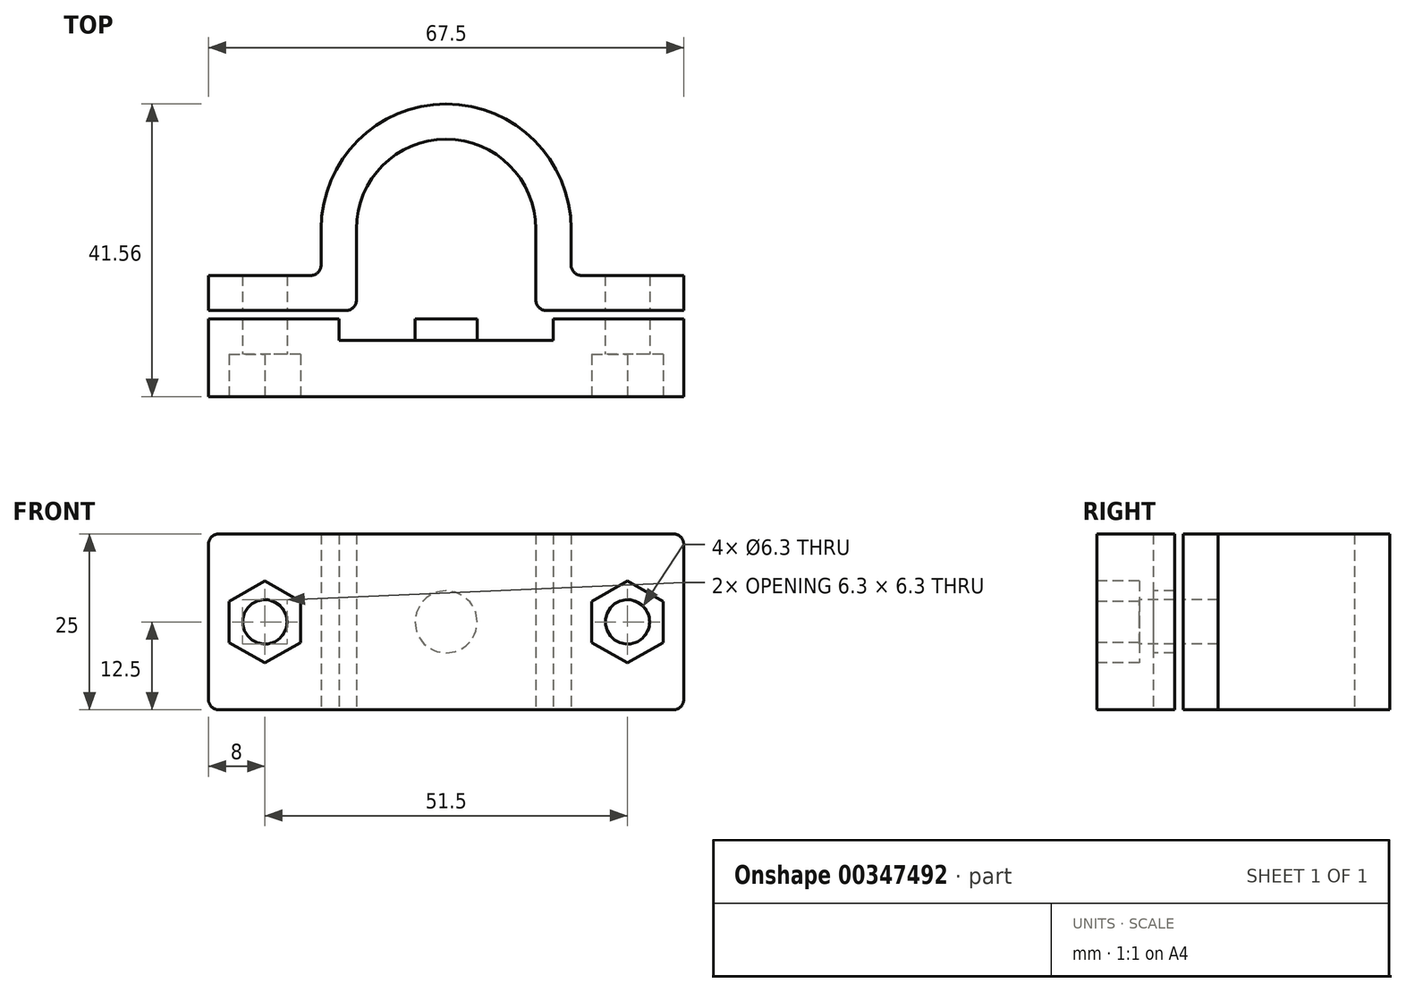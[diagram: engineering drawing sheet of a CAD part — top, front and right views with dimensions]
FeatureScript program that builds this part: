
annotation { "Feature Type Name" : "Feature", "Feature Type Description" : "" }
export const myFeature = defineFeature(function(context is Context, id is Id, definition is map)
    precondition{}
    {
        {
            var Q0;
            Q0=qCreatedBy(makeId("Top.planeOp"),FACE);
            var sketch = newSketch(context, id + "F0", { "sketchPlane" : qUnion([Q0])});
            skArc(sketch, "E0", {"start": v(12.75, 3.02) * mm, "mid": v(0, 15.77) * mm, "end": v(-12.75, 3.03) * mm});
            skLineSegment(sketch, "E1", {"start": v(-12.75, 3.02) * mm, "end": v(-12.75, -8.58) * mm});
            skLineSegment(sketch, "E2", {"start": v(-12.75, -8.58) * mm, "end": v(-33.75, -8.57) * mm});
            skLineSegment(sketch, "E3", {"start": v(-33.75, -8.57) * mm, "end": v(-33.75, -3.58) * mm});
            skLineSegment(sketch, "E4", {"start": v(-33.75, -3.58) * mm, "end": v(-17.75, -3.58) * mm});
            skLineSegment(sketch, "E5", {"start": v(-17.75, -3.58) * mm, "end": v(-17.75, 3.02) * mm});
            skArc(sketch, "E6", {"start": v(17.75, 3.03) * mm, "mid": v(0, 20.78) * mm, "end": v(-17.75, 3.03) * mm});
            skLineSegment(sketch, "E7", {"start": v(17.75, 3.03) * mm, "end": v(17.75, -3.58) * mm});
            skLineSegment(sketch, "E8", {"start": v(17.75, -3.58) * mm, "end": v(33.75, -3.58) * mm});
            skLineSegment(sketch, "E9", {"start": v(33.75, -3.58) * mm, "end": v(33.75, -8.57) * mm});
            skLineSegment(sketch, "E10", {"start": v(33.75, -8.57) * mm, "end": v(12.75, -8.58) * mm});
            skLineSegment(sketch, "E11", {"start": v(12.75, -8.58) * mm, "end": v(12.75, 3.02) * mm});
            skLineSegment(sketch, "E12", {"start": v(-33.75, -9.78) * mm, "end": v(-15.2, -9.78) * mm});
            skLineSegment(sketch, "E13", {"start": v(-15.2, -9.78) * mm, "end": v(-15.2, -12.78) * mm});
            skLineSegment(sketch, "E14", {"start": v(-15.2, -12.78) * mm, "end": v(15.2, -12.78) * mm});
            skLineSegment(sketch, "E15", {"start": v(15.2, -12.78) * mm, "end": v(15.2, -9.78) * mm});
            skLineSegment(sketch, "E16", {"start": v(15.2, -9.78) * mm, "end": v(33.75, -9.77) * mm});
            skLineSegment(sketch, "E17", {"start": v(33.75, -9.77) * mm, "end": v(33.75, -20.77) * mm});
            skLineSegment(sketch, "E18", {"start": v(33.75, -20.77) * mm, "end": v(-33.75, -20.78) * mm});
            skLineSegment(sketch, "E19", {"start": v(-33.75, -20.78) * mm, "end": v(-33.75, -9.78) * mm});
            skSolve(sketch);
        }
        {
            var Q0;
            Q0=makeQuery(id+"F0.imprint","IMPRINT",FACE,{"disambiguationData":[TD([[makeQuery(id+"F0.imprint","IMPRINT",EDGE,{"derivedFrom":sQuery(id+"F0.wireOp",EDGE,"E0")}),-1.0]])]});
            var Q1;
            Q1=makeQuery(id+"F0.imprint","IMPRINT",FACE,{"disambiguationData":[TD([[makeQuery(id+"F0.imprint","IMPRINT",EDGE,{"derivedFrom":sQuery(id+"F0.wireOp",EDGE,"E12")}),-1.0]])]});
            extrude(context, id + "F1", {"entities" : qUnion([Q0, Q1]), "depth" : 25 * mm});
        }
        {
            var Q0;
            Q0=makeQuery(id+"F1.opExtrude","SWEPT_FACE",FACE,{"disambiguationData":[OSD([sQuery(id+"F0.wireOp",EDGE,"E18")])]});
            var sketch = newSketch(context, id + "F2", { "sketchPlane" : qUnion([Q0])});
            skCircle(sketch, "E20", {"center": v(-25.75, 12.5) * mm, "radius": 3.15 * mm});
            skCircle(sketch, "E21", {"center": v(25.75, 12.5) * mm, "radius": 3.15 * mm});
            skSolve(sketch);
        }
        {
            var Q0;
            Q0=makeQuery(id+"F2.imprint","IMPRINT",FACE,{"disambiguationData":[TD([[makeQuery(id+"F2.imprint","IMPRINT",EDGE,{"derivedFrom":sQuery(id+"F2.wireOp",EDGE,"E20")}),1.0]])]});
            var Q1;
            Q1=makeQuery(id+"F2.imprint","IMPRINT",FACE,{"disambiguationData":[TD([[makeQuery(id+"F2.imprint","IMPRINT",EDGE,{"derivedFrom":sQuery(id+"F2.wireOp",EDGE,"E21")}),1.0]])]});
            extrude(context, id + "F3", {"entities" : qUnion([Q0, Q1]), "operationType" : NewBodyOperationType.REMOVE, "oppositeDirection" : true, "depth" : 25 * mm});
        }
        {
            var Q0;
            Q0=makeQuery(id+"F1.opExtrude","SWEPT_FACE",FACE,{"disambiguationData":[OSD([sQuery(id+"F0.wireOp",EDGE,"E14")])]});
            var sketch = newSketch(context, id + "F4", { "sketchPlane" : qUnion([Q0])});
            skCircle(sketch, "E22", {"center": v(0, 12.5) * mm, "radius": 4.4 * mm});
            skSolve(sketch);
        }
        {
            var Q0;
            Q0=makeQuery(id+"F4.imprint","IMPRINT",FACE,{"disambiguationData":[TD([[makeQuery(id+"F4.imprint","IMPRINT",EDGE,{"derivedFrom":sQuery(id+"F4.wireOp",EDGE,"E22")}),1.0]])]});
            extrude(context, id + "F5", {"entities" : qUnion([Q0]), "operationType" : NewBodyOperationType.ADD, "depth" : 3 * mm});
        }
        {
            var Q0;
            Q0=makeQuery(id+"F1.opExtrude","SWEPT_FACE",FACE,{"disambiguationData":[OSD([sQuery(id+"F0.wireOp",EDGE,"E2")])]});
            var sketch = newSketch(context, id + "F6", { "sketchPlane" : qUnion([Q0])});
            skCircle(sketch, "E23", {"center": v(25.75, 12.5) * mm, "radius": 3.1 * mm});
            skCircle(sketch, "E24", {"center": v(-25.75, 12.5) * mm, "radius": 3.1 * mm});
            skSolve(sketch);
        }
        {
            var Q0;
            Q0=makeQuery(id+"F6.imprint","IMPRINT",FACE,{"disambiguationData":[TD([[makeQuery(id+"F6.imprint","IMPRINT",EDGE,{"derivedFrom":sQuery(id+"F6.wireOp",EDGE,"E24")}),1.0]])]});
            var Q1;
            Q1=makeQuery(id+"F6.imprint","IMPRINT",FACE,{"disambiguationData":[TD([[makeQuery(id+"F6.imprint","IMPRINT",EDGE,{"derivedFrom":sQuery(id+"F6.wireOp",EDGE,"E23")}),1.0]])]});
            extrude(context, id + "F7", {"entities" : qUnion([Q0, Q1]), "operationType" : NewBodyOperationType.REMOVE, "oppositeDirection" : true, "depth" : 25 * mm});
        }
        {
            var Q0;
            Q0=makeQuery(id+"F1.opExtrude","SWEPT_EDGE",EDGE,{"disambiguationData":[OSD([sQuery(id+"F0.wireOp",EDGE,"E4"),sQuery(id+"F0.wireOp",EDGE,"E5")])]});
            var Q1;
            Q1=makeQuery(id+"F1.opExtrude","SWEPT_EDGE",EDGE,{"disambiguationData":[OSD([sQuery(id+"F0.wireOp",EDGE,"E7"),sQuery(id+"F0.wireOp",EDGE,"E8")])]});
            var Q2;
            Q2=makeQuery(id+"F1.opExtrude","CAP_EDGE",EDGE,{"disambiguationData":[OSD([sQuery(id+"F0.wireOp",EDGE,"E9")])],"isStart":false});
            var Q3;
            Q3=makeQuery(id+"F1.opExtrude","CAP_EDGE",EDGE,{"disambiguationData":[OSD([sQuery(id+"F0.wireOp",EDGE,"E9")])],"isStart":true});
            var Q4;
            Q4=makeQuery(id+"F1.opExtrude","CAP_EDGE",EDGE,{"disambiguationData":[OSD([sQuery(id+"F0.wireOp",EDGE,"E3")])],"isStart":true});
            var Q5;
            Q5=makeQuery(id+"F1.opExtrude","CAP_EDGE",EDGE,{"disambiguationData":[OSD([sQuery(id+"F0.wireOp",EDGE,"E3")])],"isStart":false});
            var Q6;
            Q6=makeQuery(id+"F1.opExtrude","SWEPT_EDGE",EDGE,{"disambiguationData":[OSD([sQuery(id+"F0.wireOp",EDGE,"E1"),sQuery(id+"F0.wireOp",EDGE,"E2")])]});
            var Q7;
            Q7=makeQuery(id+"F1.opExtrude","SWEPT_EDGE",EDGE,{"disambiguationData":[OSD([sQuery(id+"F0.wireOp",EDGE,"E10"),sQuery(id+"F0.wireOp",EDGE,"E11")])]});
            fillet(context, id + "F8", {"entities" : qUnion([Q0, Q1, Q2, Q3, Q4, Q5, Q6, Q7]), "radius" : 1.5 * mm, "tangentPropagation" : true, "allowEdgeOverflow" : false});
        }
        {
            var Q0;
            Q0=makeQuery(id+"F1.opExtrude","CAP_EDGE",EDGE,{"disambiguationData":[OSD([sQuery(id+"F0.wireOp",EDGE,"E17")])],"isStart":false});
            var Q1;
            Q1=makeQuery(id+"F1.opExtrude","CAP_EDGE",EDGE,{"disambiguationData":[OSD([sQuery(id+"F0.wireOp",EDGE,"E17")])],"isStart":true});
            var Q2;
            Q2=makeQuery(id+"F1.opExtrude","CAP_EDGE",EDGE,{"disambiguationData":[OSD([sQuery(id+"F0.wireOp",EDGE,"E19")])],"isStart":false});
            var Q3;
            Q3=makeQuery(id+"F1.opExtrude","CAP_EDGE",EDGE,{"disambiguationData":[OSD([sQuery(id+"F0.wireOp",EDGE,"E19")])],"isStart":true});
            fillet(context, id + "F9", {"entities" : qUnion([Q0, Q1, Q2, Q3]), "radius" : 1.5 * mm, "tangentPropagation" : true, "allowEdgeOverflow" : false});
        }
        {
            var Q0;
            Q0=makeQuery(id+"F1.opExtrude","SWEPT_FACE",FACE,{"disambiguationData":[OSD([sQuery(id+"F0.wireOp",EDGE,"E18")])]});
            var sketch = newSketch(context, id + "F10", { "sketchPlane" : qUnion([Q0])});
            skCircle(sketch, "E25.cCircle", {"center": v(-25.75, 12.5) * mm, "radius": 5.05 * mm, "construction": true});
            skLineSegment(sketch, "E25.0", {"start": v(-20.7, 9.58) * mm, "end": v(-25.75, 6.67) * mm});
            skLineSegment(sketch, "E25.1", {"start": v(-25.75, 6.67) * mm, "end": v(-30.8, 9.58) * mm});
            skLineSegment(sketch, "E25.2", {"start": v(-30.8, 9.58) * mm, "end": v(-30.8, 15.42) * mm});
            skLineSegment(sketch, "E25.3", {"start": v(-30.8, 15.42) * mm, "end": v(-25.75, 18.33) * mm});
            skLineSegment(sketch, "E25.4", {"start": v(-25.75, 18.33) * mm, "end": v(-20.7, 15.42) * mm});
            skLineSegment(sketch, "E25.5", {"start": v(-20.7, 15.42) * mm, "end": v(-20.7, 9.58) * mm});
            skPoint(sketch, "E25.0.midPoint", {"position": v(-23.23, 8.13) * mm});
            skCircle(sketch, "E26.cCircle", {"center": v(25.75, 12.5) * mm, "radius": 5.05 * mm, "construction": true});
            skLineSegment(sketch, "E26.0", {"start": v(30.8, 9.58) * mm, "end": v(25.75, 6.67) * mm});
            skLineSegment(sketch, "E26.1", {"start": v(25.75, 6.67) * mm, "end": v(20.7, 9.58) * mm});
            skLineSegment(sketch, "E26.2", {"start": v(20.7, 9.58) * mm, "end": v(20.7, 15.42) * mm});
            skLineSegment(sketch, "E26.3", {"start": v(20.7, 15.42) * mm, "end": v(25.75, 18.33) * mm});
            skLineSegment(sketch, "E26.4", {"start": v(25.75, 18.33) * mm, "end": v(30.8, 15.42) * mm});
            skLineSegment(sketch, "E26.5", {"start": v(30.8, 15.42) * mm, "end": v(30.8, 9.58) * mm});
            skPoint(sketch, "E26.0.midPoint", {"position": v(28.27, 8.13) * mm});
            skSolve(sketch);
        }
        {
            var Q0;
            Q0=makeQuery(id+"F10.imprint","IMPRINT",FACE,{"disambiguationData":[TD([[makeQuery(id+"F10.imprint","IMPRINT",EDGE,{"derivedFrom":sQuery(id+"F10.wireOp",EDGE,"E25.0")}),-1.0]])]});
            var Q1;
            Q1=makeQuery(id+"F10.imprint","IMPRINT",FACE,{"disambiguationData":[TD([[makeQuery(id+"F10.imprint","IMPRINT",EDGE,{"derivedFrom":sQuery(id+"F10.wireOp",EDGE,"E26.0")}),-1.0]])]});
            extrude(context, id + "F11", {"entities" : qUnion([Q0, Q1]), "operationType" : NewBodyOperationType.REMOVE, "oppositeDirection" : true, "depth" : 6 * mm});
        }
    });
